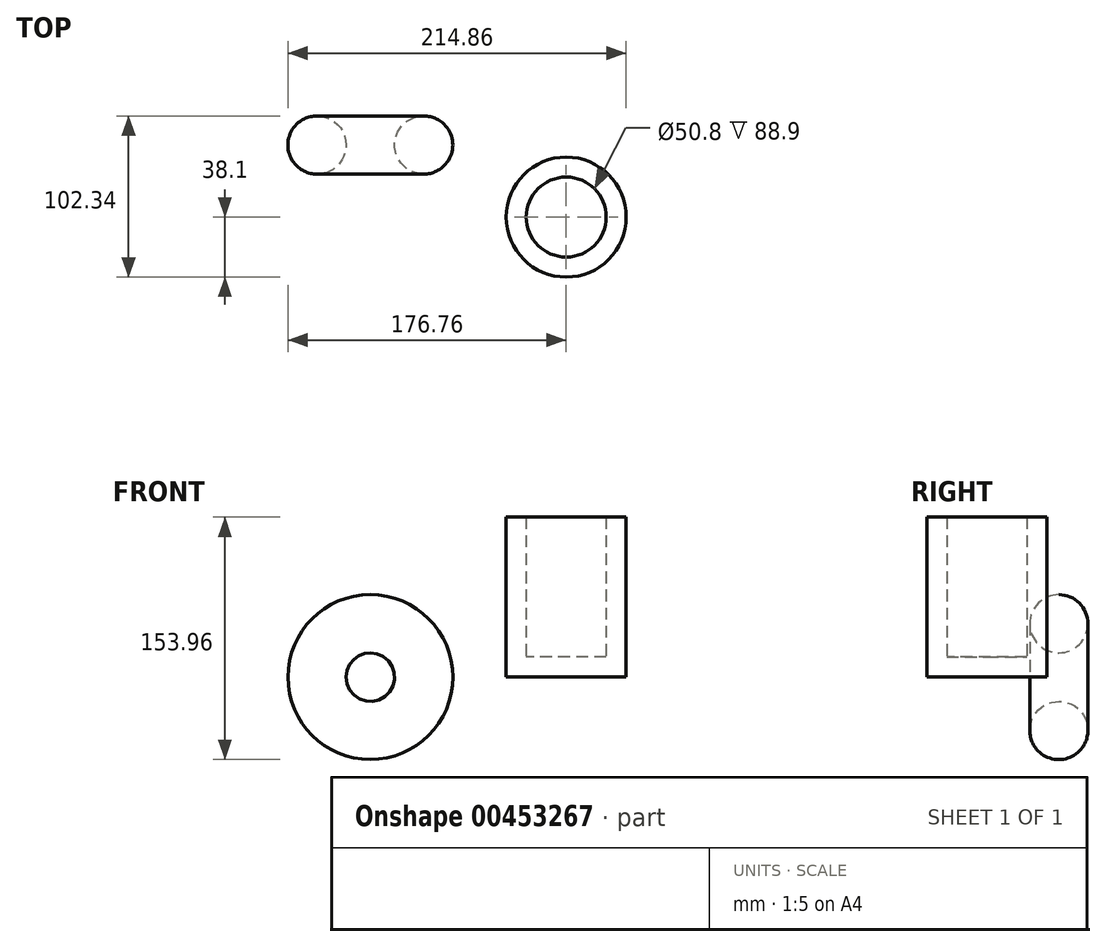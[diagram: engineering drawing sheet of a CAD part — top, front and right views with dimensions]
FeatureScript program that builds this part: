
annotation { "Feature Type Name" : "Feature", "Feature Type Description" : "" }
export const myFeature = defineFeature(function(context is Context, id is Id, definition is map)
    precondition{}
    {
        {
            var Q0;
            Q0=qCreatedBy(makeId("Top.planeOp"),FACE);
            var sketch = newSketch(context, id + "F0", { "sketchPlane" : qUnion([Q0])});
            skCircle(sketch, "E0", {"center": v(0, 0) * mm, "radius": 38.1 * mm});
            skSolve(sketch);
        }
        {
            var Q0;
            Q0 = qSketchRegion(id + "F0", true);
            extrude(context, id + "F1", {"entities" : qUnion([Q0]), "depth" : 101.6 * mm});
        }
        {
            var Q0;
            Q0=makeQuery(id+"F1.opExtrude","CAP_FACE",FACE,{"disambiguationData":[OSD([sQuery(id+"F0.wireOp",EDGE,"E0")])],"isStart":false});
            shell(context, id + "F2", {"entities" : qUnion([Q0]), "thickness" : 12.7 * mm});
        }
        {
            var Q0;
            Q0=qCreatedBy(makeId("Top.planeOp"),FACE);
            var sketch = newSketch(context, id + "F3", { "sketchPlane" : qUnion([Q0])});
            skCircle(sketch, "E1", {"center": v(-90.5, 45.78) * mm, "radius": 18.46 * mm});
            skLineSegment(sketch, "E2", {"start": v(-90.5, 66.97) * mm, "end": v(-90.5, 20.4) * mm, "construction": true});
            skLineSegment(sketch, "E3", {"start": v(-124.4, 66.85) * mm, "end": v(-124.4, 21.14) * mm, "construction": true});
            skSolve(sketch);
        }
        {
            var Q0;
            Q0=makeQuery(id+"F3.imprint","IMPRINT",FACE,{"disambiguationData":[TD([[makeQuery(id+"F3.imprint","IMPRINT",EDGE,{"derivedFrom":sQuery(id+"F3.wireOp",EDGE,"E1")}),1.0]])]});
            var Q1;
            Q1=sQuery(id+"F3.wireOp",EDGE,"E3");
            revolve(context, id + "F4", {"entities" : qUnion([Q0]), "axis" : qUnion([Q1]), "revolveType" : RevolveType.FULL});
        }
    });
